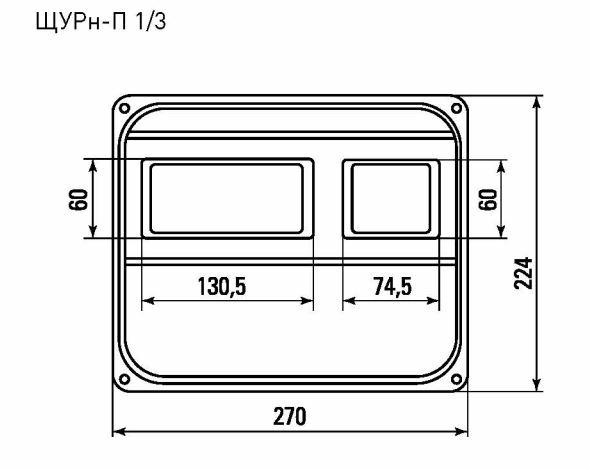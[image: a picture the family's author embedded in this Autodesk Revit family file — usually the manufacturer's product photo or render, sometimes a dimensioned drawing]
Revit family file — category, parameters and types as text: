
# Revit family: EKF_EE_ЯУР_Без_Задней_Стенки_Basic
name_source: partatom
category: Электрооборудование
units: mm (PartAtom-declared; Revit-internal decimal feet)

## family parameters
Всегда вертикально = Да
На основе рабочей плоскости = Нет
Общий = Нет
При загрузке вырезать с полостями = Нет
Размер круглого соединителя = Использовать диаметр
Тип детали = Силовой щит
Точка расчета площади = Да

## types (3) — shared parameters
ADSK_Единица измерения = компл.
ADSK_Завод-изготовитель = EKF
ADSK_Классификация нагрузок = Прочее
ADSK_Количество = 1
ADSK_Количество фаз = 3
ADSK_Коэффициент мощности = 1
ADSK_Материал = RAL 7035_Сталь
ADSK_Напряжение = 400 В
ADSK_Номинальная мощность = 0 Вт
ADSK_Полная мощность = 0 В·А
ADSK_Размер_Глубина = 150 мм
ADSK_Размер_Ширина = 300 мм
ADSK_Ток = 125 А
Изготовитель = EKF
Количество DIN-реек = 1
Количество модулей на DIN-рейке = 12
Максимальное количество модулей = 12
Серия номенклатуры = Basic
Степень защиты IP = IP31
ТВ = EKF
Тип установки = Навесной
zero-valued in all types: ADSK_Масса

## per-type parameters (varying)
| type | ADSK_Код изделия | ADSK_Марка | ADSK_Наименование | ADSK_Обозначение | ADSK_Размер_Высота | Описание | Тип |
| ЯУР с двумя DIN-рейками без задней стенки (400х300х150) EKF Basic | uerm2-din-400-bas | ЯУР с двумя DIN-рейками | ЯУР с двумя DIN-рейками (400х300х150) EKF BasicЯУР с двумя DIN-рейками (400х300х150) EKF Basic | ЯУР с двумя DIN-рейками | 400 мм | ЯУР с двумя DIN-рейками (400х300х150) EKF BasicЯУР с двумя DIN-рейками (400х300х150) EKF Basic | 214 мм |
| ЯУР с одной DIN-рейкой без задней стенки (300х300х150) EKF Basic | uerm2-din-300-bas | ЯУР с одной DIN-рейкой | ЯУР с одной DIN-рейкой (300х300х150) EKF BasicЯУР с одной DIN-рейкой (300х300х150) EKF Basic | ЯУР с одной DIN-рейкой | 300 мм | ЯУР с одной DIN-рейкой (300х300х150) EKF BasicЯУР с одной DIN-рейкой (300х300х150) EKF Basic | 215 мм |
| ЯУР с тремя DIN-рейками без задней стенки (600х300х150) EKF Basic | uerm2-din-600-bas | ЯУР с тремя DIN-рейками | ЯУР с тремя DIN-рейками (600х300х150) EKF BasicЯУР с тремя DIN-рейками (600х300х150) EKF Basic | ЯУР с тремя DIN-рейками | 600 мм | ЯУР с тремя DIN-рейками (600х300х150) EKF BasicЯУР с тремя DIN-рейками (600х300х150) EKF Basic | 216 мм |
